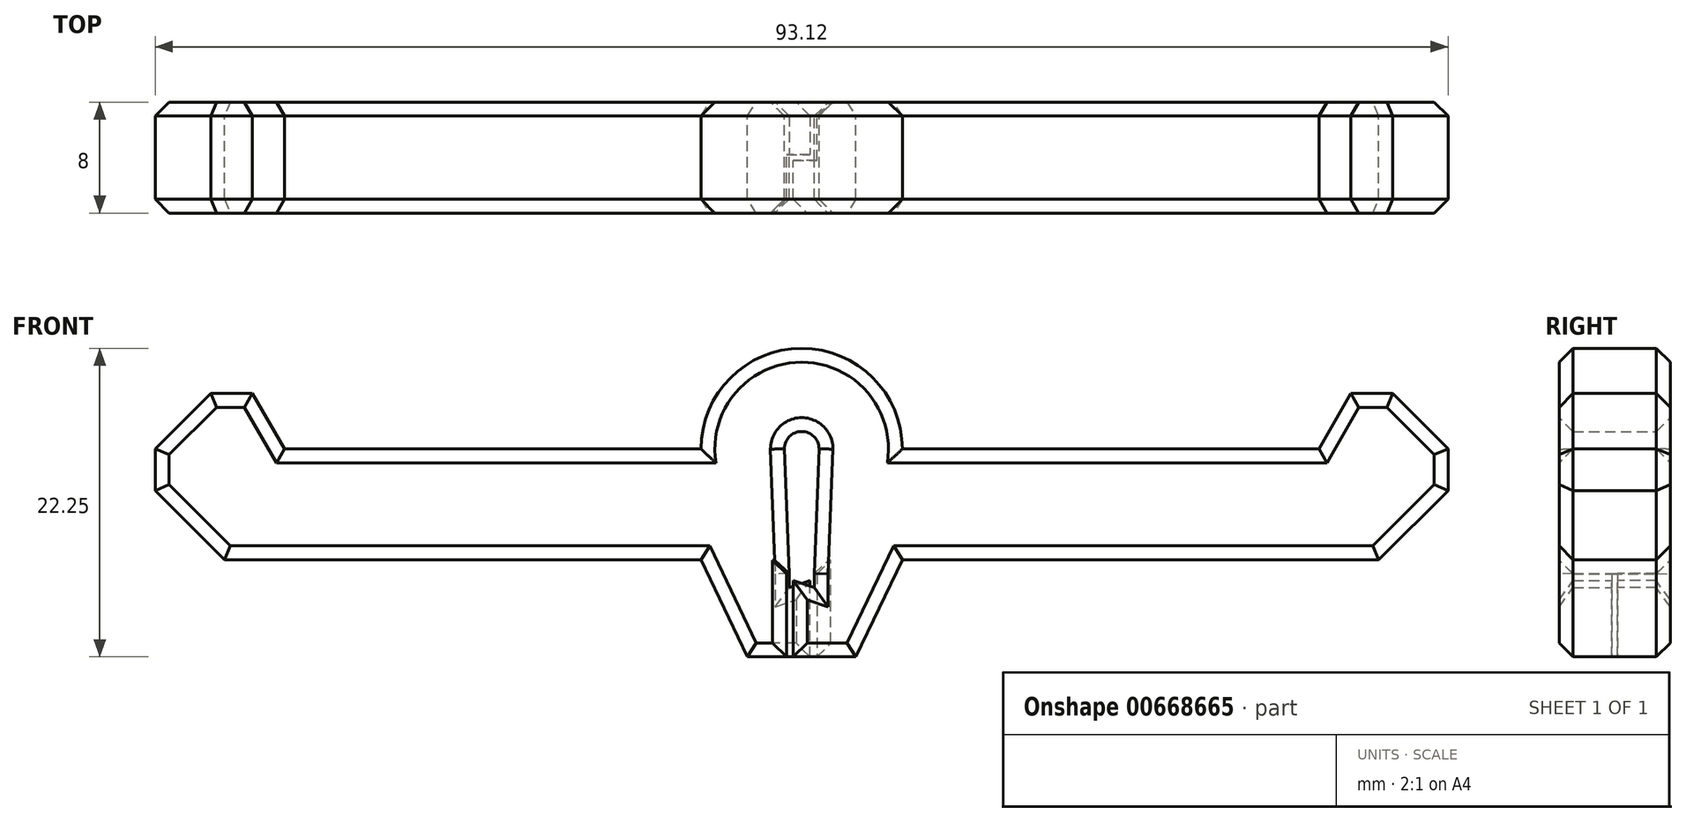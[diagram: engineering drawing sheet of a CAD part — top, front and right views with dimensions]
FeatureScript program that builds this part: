
annotation { "Feature Type Name" : "Feature", "Feature Type Description" : "" }
export const myFeature = defineFeature(function(context is Context, id is Id, definition is map)
    precondition{}
    {
        {
            var Q0;
            Q0=qCreatedBy(makeId("Front.planeOp"),FACE);
            var sketch = newSketch(context, id + "F0", { "sketchPlane" : qUnion([Q0])});
            skLineSegment(sketch, "E0", {"start": v(7.25, 0) * mm, "end": v(37.25, 0) * mm});
            skLineSegment(sketch, "E1", {"start": v(37.25, 0) * mm, "end": v(39.56, 4) * mm});
            skLineSegment(sketch, "E2", {"start": v(39.56, 4) * mm, "end": v(42.56, 4) * mm});
            skLineSegment(sketch, "E3", {"start": v(42.56, 4) * mm, "end": v(46.56, 0) * mm});
            skLineSegment(sketch, "E4", {"start": v(46.56, 0) * mm, "end": v(46.56, -3) * mm});
            skLineSegment(sketch, "E5", {"start": v(41.56, -8) * mm, "end": v(7.25, -8) * mm});
            skLineSegment(sketch, "E6", {"start": v(7.25, -8) * mm, "end": v(3.9, -15) * mm});
            skLineSegment(sketch, "E7", {"start": v(3.9, -15) * mm, "end": v(-0.6, -15) * mm});
            skLineSegment(sketch, "E8", {"start": v(-0.6, -15) * mm, "end": v(-0.6, -9.5) * mm});
            skLineSegment(sketch, "E9", {"start": v(-0.6, -9.5) * mm, "end": v(0.9, -10) * mm});
            skArc(sketch, "E10", {"start": v(-7.25, 0) * mm, "mid": v(0, 7.25) * mm, "end": v(7.25, 0) * mm});
            skArc(sketch, "E11", {"start": v(1.25, 0) * mm, "mid": v(0, 1.25) * mm, "end": v(-1.25, 0) * mm});
            skLineSegment(sketch, "E12", {"start": v(1.25, 0) * mm, "end": v(0.9, -9) * mm});
            skLineSegment(sketch, "E13.MirrorCS", {"start": v(-7.25, 0) * mm, "end": v(-37.25, 0) * mm});
            skLineSegment(sketch, "E14.MirrorCS", {"start": v(-37.25, 0) * mm, "end": v(-39.56, 4) * mm});
            skLineSegment(sketch, "E15.MirrorCS", {"start": v(-39.56, 4) * mm, "end": v(-42.56, 4) * mm});
            skLineSegment(sketch, "E16.MirrorCS", {"start": v(-1.25, 0) * mm, "end": v(-0.9, -9) * mm});
            skLineSegment(sketch, "E17.MirrorCS", {"start": v(-42.56, 4) * mm, "end": v(-46.56, 0) * mm});
            skLineSegment(sketch, "E18.MirrorCS", {"start": v(-46.56, 0) * mm, "end": v(-46.56, -3) * mm});
            skLineSegment(sketch, "E19.MirrorCS", {"start": v(-7.25, -8) * mm, "end": v(-3.9, -15) * mm});
            skLineSegment(sketch, "E20.MirrorCS", {"start": v(-41.56, -8) * mm, "end": v(-7.25, -8) * mm});
            skLineSegment(sketch, "E21", {"start": v(0.9, -9) * mm, "end": v(0.9, -10) * mm});
            skLineSegment(sketch, "E22", {"start": v(-0.9, -9) * mm, "end": v(-1.1, -9) * mm});
            skLineSegment(sketch, "E23", {"start": v(-1.1, -9) * mm, "end": v(-1.1, -15) * mm});
            skLineSegment(sketch, "E24", {"start": v(-1.1, -15) * mm, "end": v(-3.9, -15) * mm});
            skLineSegment(sketch, "E25", {"start": v(-46.56, -3) * mm, "end": v(-41.56, -8) * mm});
            skLineSegment(sketch, "E26", {"start": v(41.56, -8) * mm, "end": v(46.56, -3) * mm});
            skLineSegment(sketch, "E27", {"start": v(0, -31.1) * mm, "end": v(0, 21.1) * mm, "construction": true});
            skLineSegment(sketch, "E28.MirrorCS", {"start": v(0.9, -9) * mm, "end": v(1.1, -9) * mm});
            skLineSegment(sketch, "E29.MirrorCS", {"start": v(1.1, -9) * mm, "end": v(1.1, -15) * mm});
            skSolve(sketch);
        }
        {
            var Q0;
            Q0 = qSketchRegion(id + "F0", true);
            extrude(context, id + "F1", {"entities" : qUnion([Q0]), "depth" : 4 * mm, "offsetDistance" : 25 * mm});
        }
        {
            var Q0;
            Q0=makeQuery(id+"F1.opExtrude","CAP_FACE",FACE,{"disambiguationData":[OSD([sQuery(id+"F0.wireOp",EDGE,"E0"),sQuery(id+"F0.wireOp",EDGE,"E1"),sQuery(id+"F0.wireOp",EDGE,"E2"),sQuery(id+"F0.wireOp",EDGE,"E3"),sQuery(id+"F0.wireOp",EDGE,"E4"),sQuery(id+"F0.wireOp",EDGE,"E5"),sQuery(id+"F0.wireOp",EDGE,"E6"),sQuery(id+"F0.wireOp",EDGE,"E7"),sQuery(id+"F0.wireOp",EDGE,"E8"),sQuery(id+"F0.wireOp",EDGE,"E9"),sQuery(id+"F0.wireOp",EDGE,"E10"),sQuery(id+"F0.wireOp",EDGE,"E11"),sQuery(id+"F0.wireOp",EDGE,"E12"),sQuery(id+"F0.wireOp",EDGE,"E13.MirrorCS"),sQuery(id+"F0.wireOp",EDGE,"E14.MirrorCS"),sQuery(id+"F0.wireOp",EDGE,"E15.MirrorCS"),sQuery(id+"F0.wireOp",EDGE,"E16.MirrorCS"),sQuery(id+"F0.wireOp",EDGE,"E17.MirrorCS"),sQuery(id+"F0.wireOp",EDGE,"E18.MirrorCS"),sQuery(id+"F0.wireOp",EDGE,"E19.MirrorCS"),sQuery(id+"F0.wireOp",EDGE,"E20.MirrorCS"),sQuery(id+"F0.wireOp",EDGE,"E21"),sQuery(id+"F0.wireOp",EDGE,"E22"),sQuery(id+"F0.wireOp",EDGE,"E23"),sQuery(id+"F0.wireOp",EDGE,"E24"),sQuery(id+"F0.wireOp",EDGE,"E25"),sQuery(id+"F0.wireOp",EDGE,"E26")])],"isStart":false});
            chamfer(context, id + "F2", {"entities" : qUnion([Q0]), "width" : 1 * mm, "tangentPropagation" : true});
        }
        {
            var Q0;
            {var subQ0=sQuery(id+"F0.wireOp",EDGE,"E8");Q0=makeQuery(id+"F0.imprint","IMPRINT",FACE,{"disambiguationData":[TD([[makeQuery(id+"F0.imprint","IMPRINT",EDGE,{"derivedFrom":subQ0}),-1.0]])]});}
            extrude(context, id + "F3", {"entities" : qUnion([Q0]), "operationType" : NewBodyOperationType.REMOVE, "depth" : 0.2 * mm, "offsetDistance" : 25 * mm});
        }
        {
            var Q0;
            Q0=makeQuery(id+"F1.opExtrude","SWEPT_BODY",BODY,{"disambiguationData":[OSD([sQuery(id+"F0.wireOp",EDGE,"E0"),sQuery(id+"F0.wireOp",EDGE,"E1"),sQuery(id+"F0.wireOp",EDGE,"E2"),sQuery(id+"F0.wireOp",EDGE,"E3"),sQuery(id+"F0.wireOp",EDGE,"E4"),sQuery(id+"F0.wireOp",EDGE,"E5"),sQuery(id+"F0.wireOp",EDGE,"E6"),sQuery(id+"F0.wireOp",EDGE,"E7"),sQuery(id+"F0.wireOp",EDGE,"E8"),sQuery(id+"F0.wireOp",EDGE,"E9"),sQuery(id+"F0.wireOp",EDGE,"E10"),sQuery(id+"F0.wireOp",EDGE,"E11"),sQuery(id+"F0.wireOp",EDGE,"E12"),sQuery(id+"F0.wireOp",EDGE,"E13.MirrorCS"),sQuery(id+"F0.wireOp",EDGE,"E14.MirrorCS"),sQuery(id+"F0.wireOp",EDGE,"E15.MirrorCS"),sQuery(id+"F0.wireOp",EDGE,"E16.MirrorCS"),sQuery(id+"F0.wireOp",EDGE,"E17.MirrorCS"),sQuery(id+"F0.wireOp",EDGE,"E18.MirrorCS"),sQuery(id+"F0.wireOp",EDGE,"E19.MirrorCS"),sQuery(id+"F0.wireOp",EDGE,"E20.MirrorCS"),sQuery(id+"F0.wireOp",EDGE,"E21"),sQuery(id+"F0.wireOp",EDGE,"E22"),sQuery(id+"F0.wireOp",EDGE,"E23"),sQuery(id+"F0.wireOp",EDGE,"E24"),sQuery(id+"F0.wireOp",EDGE,"E25"),sQuery(id+"F0.wireOp",EDGE,"E26")])]});
            var Q1;
            Q1=sQuery(id+"F0.wireOp",EDGE,"E27");
            circularPattern(context, id + "F4", {"operationType" : NewBodyOperationType.ADD, "entities" : qUnion([Q0]), "axis" : qUnion([Q1]), "angle" : 360 * degree, "instanceCount" : 2, "equalSpace" : true});
        }
    });
